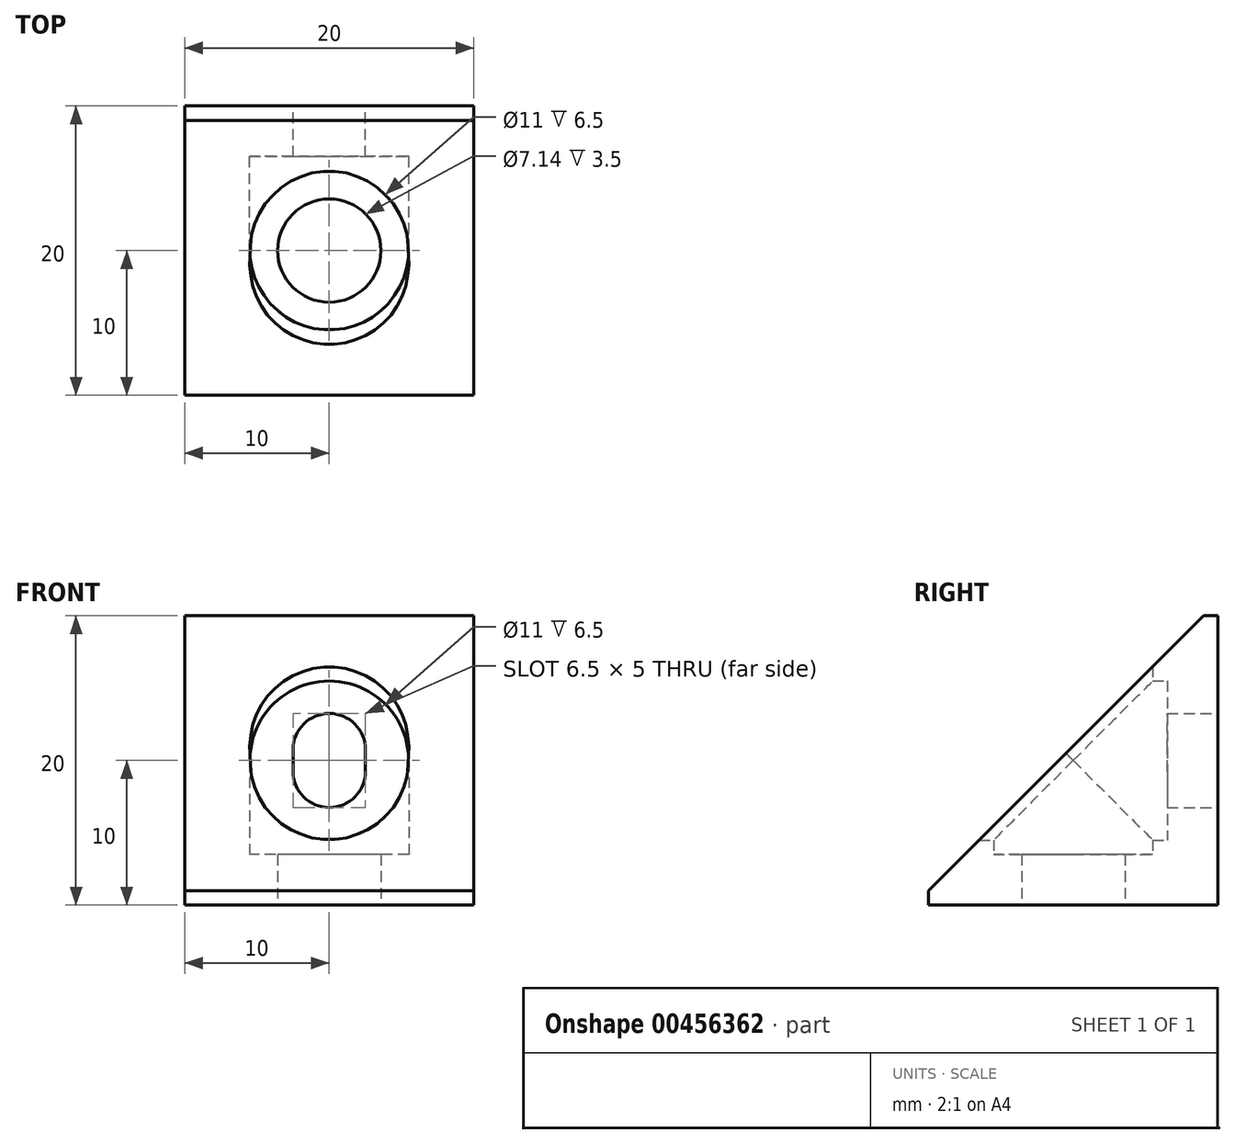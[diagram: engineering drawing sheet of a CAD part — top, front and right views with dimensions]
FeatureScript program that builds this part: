
annotation { "Feature Type Name" : "Feature", "Feature Type Description" : "" }
export const myFeature = defineFeature(function(context is Context, id is Id, definition is map)
    precondition{}
    {
        {
            var Q0;
            Q0=qCreatedBy(makeId("Top.planeOp"),FACE);
            var sketch = newSketch(context, id + "F0", { "sketchPlane" : qUnion([Q0])});
            skLineSegment(sketch, "E0.bottom", {"start": v(10, -10) * mm, "end": v(-10, -10) * mm});
            skLineSegment(sketch, "E0.top", {"start": v(10, 10) * mm, "end": v(-10, 10) * mm});
            skLineSegment(sketch, "E0.left", {"start": v(10, -10) * mm, "end": v(10, 10) * mm});
            skLineSegment(sketch, "E0.right", {"start": v(-10, -10) * mm, "end": v(-10, 10) * mm});
            skPoint(sketch, "E0.middle", {"position": v(0, 0) * mm});
            skSolve(sketch);
        }
        {
            var Q0;
            Q0=makeQuery(id+"F0.imprint","IMPRINT",FACE,{"disambiguationData":[TD([[makeQuery(id+"F0.imprint","IMPRINT",EDGE,{"derivedFrom":sQuery(id+"F0.wireOp",EDGE,"E0.bottom")}),-1.0]])]});
            extrude(context, id + "F1", {"entities" : qUnion([Q0]), "depth" : 20 * mm});
        }
        {
            var Q0;
            Q0=qCreatedBy(makeId("Top.planeOp"),FACE);
            var sketch = newSketch(context, id + "F2", { "sketchPlane" : qUnion([Q0])});
            skCircle(sketch, "E1", {"center": v(0, 0) * mm, "radius": 3.57 * mm});
            skSolve(sketch);
        }
        {
            var Q0;
            Q0 = qSketchRegion(id + "F2", true);
            extrude(context, id + "F3", {"entities" : qUnion([Q0]), "operationType" : NewBodyOperationType.REMOVE, "endBound" : BoundingType.THROUGH_ALL, "depth" : 25 * mm});
        }
        {
            var Q0;
            Q0=qCreatedBy(makeId("Top.planeOp"),FACE);
            cPlane(context, id + "F4", {"entities" : qUnion([Q0]), "cplaneType" : CPlaneType.OFFSET, "offset" : 3.5 * mm, "width" : 150 * mm, "height" : 150 * mm});
        }
        {
            var Q0;
            Q0=qCreatedBy(id+"F4.planeOp",FACE);
            var sketch = newSketch(context, id + "F5", { "sketchPlane" : qUnion([Q0])});
            skCircle(sketch, "E2", {"center": v(0, 0) * mm, "radius": 5.5 * mm});
            skSolve(sketch);
        }
        {
            var Q0;
            Q0 = qSketchRegion(id + "F5", true);
            var Q1;
            Q1=makeQuery(id+"F1.opExtrude","CAP_FACE",FACE,{"disambiguationData":[OSD([sQuery(id+"F0.wireOp",EDGE,"E0.bottom"),sQuery(id+"F0.wireOp",EDGE,"E0.top"),sQuery(id+"F0.wireOp",EDGE,"E0.left"),sQuery(id+"F0.wireOp",EDGE,"E0.right")])],"isStart":false});
            extrude(context, id + "F6", {"entities" : qUnion([Q0]), "operationType" : NewBodyOperationType.REMOVE, "endBound" : BoundingType.UP_TO_SURFACE, "endBoundEntityFace" : qUnion([Q1]), "depth" : 25 * mm});
        }
        {
            var Q0;
            Q0=makeQuery(id+"F1.opExtrude","SWEPT_FACE",FACE,{"disambiguationData":[OSD([sQuery(id+"F0.wireOp",EDGE,"E0.top")])]});
            var sketch = newSketch(context, id + "F7", { "sketchPlane" : qUnion([Q0])});
            skLineSegment(sketch, "E3", {"start": v(12.26, 10) * mm, "end": v(-10.67, 10) * mm, "construction": true});
            skPoint(sketch, "E4", {"position": v(0, 10) * mm});
            skArc(sketch, "E5", {"start": v(2.5, 10.75) * mm, "mid": v(0, 13.25) * mm, "end": v(-2.5, 10.75) * mm});
            skArc(sketch, "E6", {"start": v(-2.5, 9.25) * mm, "mid": v(0, 6.75) * mm, "end": v(2.5, 9.25) * mm});
            skLineSegment(sketch, "E7", {"start": v(2.5, 10.75) * mm, "end": v(2.5, 9.25) * mm});
            skLineSegment(sketch, "E8", {"start": v(-2.5, 10.75) * mm, "end": v(-2.5, 9.25) * mm});
            skSolve(sketch);
        }
        {
            var Q0;
            Q0 = qSketchRegion(id + "F7", true);
            extrude(context, id + "F8", {"entities" : qUnion([Q0]), "operationType" : NewBodyOperationType.REMOVE, "endBound" : BoundingType.THROUGH_ALL, "oppositeDirection" : true, "depth" : 25 * mm});
        }
        {
            var Q0;
            Q0=makeQuery(id+"F1.opExtrude","SWEPT_FACE",FACE,{"disambiguationData":[OSD([sQuery(id+"F0.wireOp",EDGE,"E0.top")])]});
            cPlane(context, id + "F9", {"entities" : qUnion([Q0]), "cplaneType" : CPlaneType.OFFSET, "offset" : 3.5 * mm, "oppositeDirection" : true, "width" : 150 * mm, "height" : 150 * mm});
        }
        {
            var Q0;
            Q0=qCreatedBy(id+"F9.planeOp",FACE);
            var sketch = newSketch(context, id + "F10", { "sketchPlane" : qUnion([Q0])});
            skCircle(sketch, "E9", {"center": v(0, 10) * mm, "radius": 5.5 * mm});
            skSolve(sketch);
        }
        {
            var Q0;
            Q0 = qSketchRegion(id + "F10", true);
            var Q1;
            Q1=makeQuery(id+"F1.opExtrude","SWEPT_FACE",FACE,{"disambiguationData":[OSD([sQuery(id+"F0.wireOp",EDGE,"E0.bottom")])]});
            extrude(context, id + "F11", {"entities" : qUnion([Q0]), "operationType" : NewBodyOperationType.REMOVE, "endBound" : BoundingType.UP_TO_SURFACE, "oppositeDirection" : true, "endBoundEntityFace" : qUnion([Q1]), "depth" : 25 * mm});
        }
        {
            var Q0;
            Q0=qCreatedBy(makeId("Right.planeOp"),FACE);
            var sketch = newSketch(context, id + "F12", { "sketchPlane" : qUnion([Q0])});
            skLineSegment(sketch, "E10", {"start": v(-10, 1) * mm, "end": v(9, 20) * mm});
            skLineSegment(sketch, "E11", {"start": v(9, 20) * mm, "end": v(-10, 20) * mm});
            skLineSegment(sketch, "E12", {"start": v(-10, 20) * mm, "end": v(-10, 1) * mm});
            skSolve(sketch);
        }
        {
            var Q0;
            Q0 = qSketchRegion(id + "F12", true);
            extrude(context, id + "F13", {"entities" : qUnion([Q0]), "operationType" : NewBodyOperationType.REMOVE, "endBound" : BoundingType.SYMMETRIC, "oppositeDirection" : true, "depth" : 25 * mm});
        }
    });
